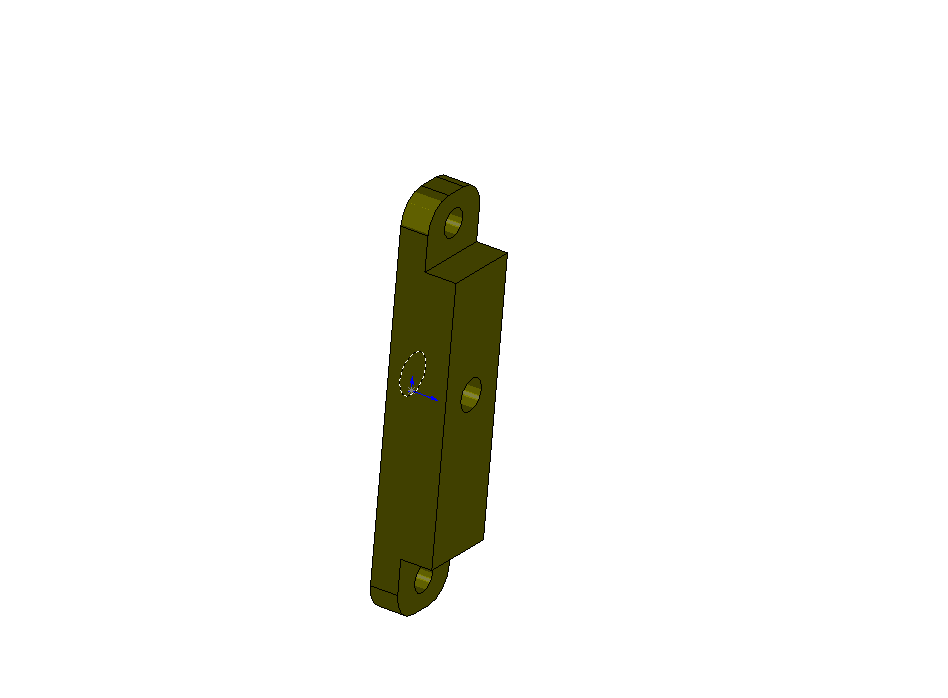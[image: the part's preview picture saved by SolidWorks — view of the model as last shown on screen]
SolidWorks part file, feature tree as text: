
SOLIDWORKS PART (.sldprt)
format: sldprt  version: not decoded by parser v0  size: 340,480 bytes
history: native  units: mm
features: sketch x6, hole x2, material x1, extrude x1, thread x1, cut_extrude x1, fillet x1 + 1 further entry (+11 scaffold rows collapsed)
feature tree (25):
  scaffold x11  (default folders/planes/origin — collapsed)
  material  "Material <not specified>"
  "Origin"  ID=-1
  sketch  "Sketch1"  dims[D1=63.5mm D2=12.7mm]
  extrude  "Extrude1"  Depth=9.525mm
  hole  "1/4-20 Tapped Hole1"  Diameter=5.1054mm Depth=9.525mm
  sketch  "Sketch5"  dims[D1=2.54mm]
  sketch  "Sketch4"  dims[hole-wizard template sketch: 60 standard entries collapsed; hole parameters kept: c18.Thru Tap Drill Depth=9.525mm]
  thread  "Cosmetic Thread1"  Diameter=6.35mm  [1 undecoded]
  hole  "#8 Clearance Hole1"  Diameter=4.4958mm Depth=9.525mm
  sketch  "Sketch3"  dims[D1=53.8mm]
  sketch  "Sketch2"  dims[hole-wizard template sketch: 60 standard entries collapsed; hole parameters kept: c18.Thru Hole Depth=9.525mm]
  sketch  "Sketch6"  dims[D1=10.0mm]
  cut_extrude  "Cut-Extrude1"  Depth=5.08mm
  fillet  "Fillet1"  Radius=4.5mm
decode coverage: 12 of 12 modeling features carry decoded parameters; 1 rows unclassified (native names shown)
note: ~ marks probable driven/reference dimensions
note: 1 parameter value undecoded
note: suppression state not decoded; provenance and decode notes live in map.json
